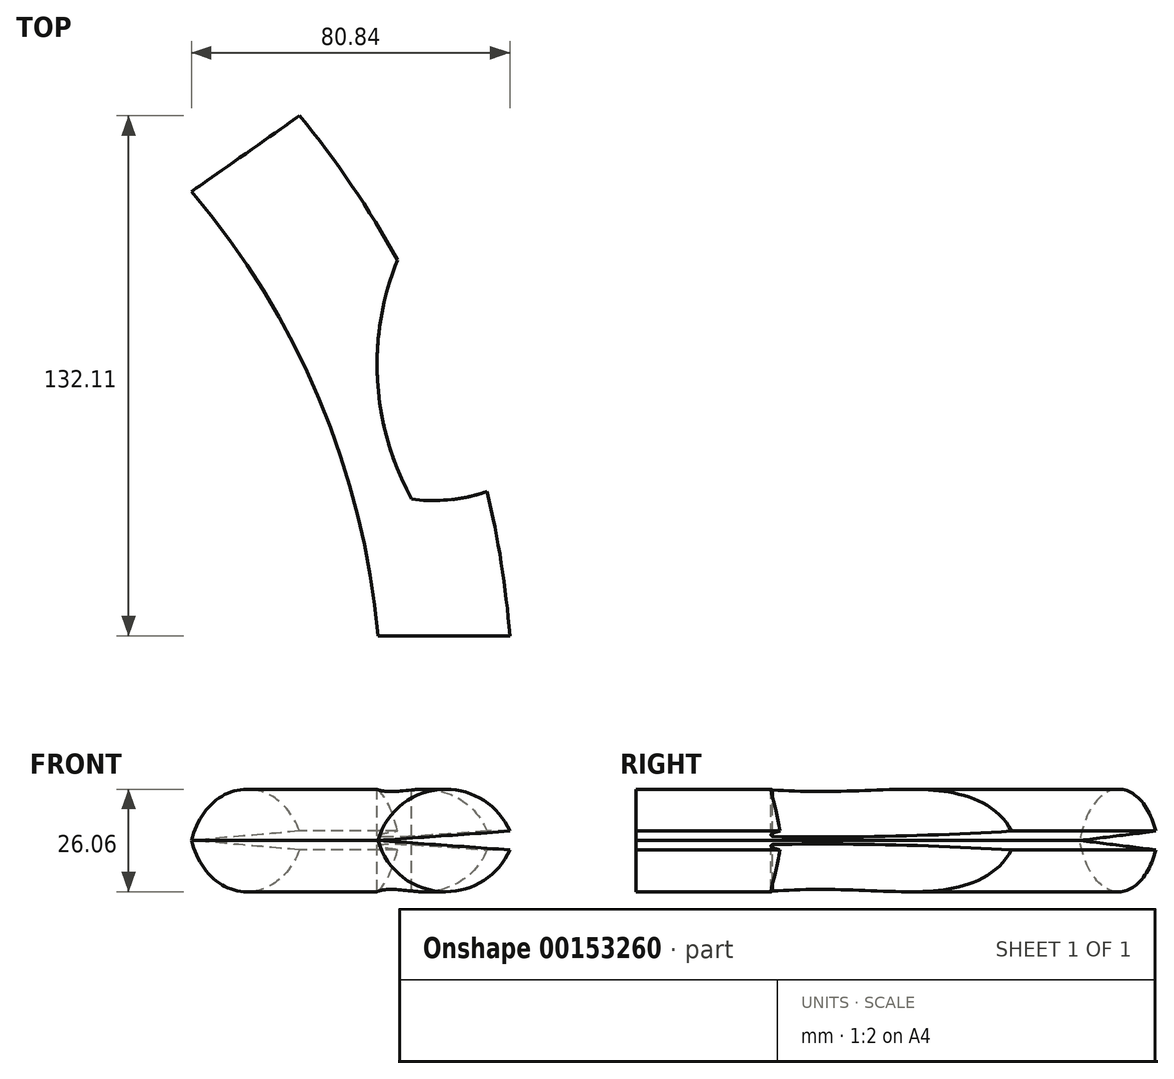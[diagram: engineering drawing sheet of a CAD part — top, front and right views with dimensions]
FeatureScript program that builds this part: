
annotation { "Feature Type Name" : "Feature", "Feature Type Description" : "" }
export const myFeature = defineFeature(function(context is Context, id is Id, definition is map)
    precondition{}
    {
        {
            var Q0;
            Q0=qCreatedBy(makeId("Front.planeOp"),FACE);
            var sketch = newSketch(context, id + "F0", { "sketchPlane" : qUnion([Q0])});
            skArc(sketch, "E0", {"start": v(19.52, 2.39) * mm, "mid": v(1.94, 12.98) * mm, "end": v(-13.96, 0) * mm});
            skLineSegment(sketch, "E1", {"start": v(19.52, 2.39) * mm, "end": v(-13.96, 0) * mm});
            skSolve(sketch);
        }
        {
            var Q0;
            Q0=qCreatedBy(makeId("Top.planeOp"),FACE);
            var sketch = newSketch(context, id + "F1", { "sketchPlane" : qUnion([Q0])});
            skArc(sketch, "E2", {"start": v(55.51, 105.68) * mm, "mid": v(16.55, 59.1) * mm, "end": v(2.58, 0) * mm});
            skArc(sketch, "E3", {"start": v(2.58, 0) * mm, "mid": v(-13.16, 65.07) * mm, "end": v(-47.79, 122.36) * mm});
            skSolve(sketch);
        }
        {
            var Q0;
            Q0=makeQuery(id+"F0.imprint","IMPRINT",FACE,{"disambiguationData":[TD([[makeQuery(id+"F0.imprint","IMPRINT",EDGE,{"derivedFrom":sQuery(id+"F0.wireOp",EDGE,"E0")}),1.0]])]});
            var Q1;
            Q1=sQuery(id+"F1.wireOp",EDGE,"E3");
            sweep(context, id + "F2", {"profiles" : qUnion([Q0]), "path" : qUnion([Q1])});
        }
        {
            var Q0;
            Q0=makeQuery(id+"F2.opSweep","SWEPT_BODY",BODY,{"disambiguationData":[OSD([sQuery(id+"F0.wireOp",EDGE,"E0"),sQuery(id+"F0.wireOp",EDGE,"E1"),sQuery(id+"F1.wireOp",EDGE,"E3")])]});
            var Q1;
            Q1=qCreatedBy(makeId("Top.planeOp"),FACE);
            mirror(context, id + "F3", {"entities" : qUnion([Q0]), "mirrorPlane" : qUnion([Q1])});
        }
        {
            var Q0;
            Q0=qCreatedBy(makeId("Top.planeOp"),FACE);
            var sketch = newSketch(context, id + "F4", { "sketchPlane" : qUnion([Q0])});
            skArc(sketch, "E4", {"start": v(2.34, 114.47) * mm, "mid": v(-13.86, 75.8) * mm, "end": v(-5.43, 34.71) * mm});
            skArc(sketch, "E5", {"start": v(-5.43, 34.71) * mm, "mid": v(26.96, 44.14) * mm, "end": v(41.75, 74.45) * mm});
            skArc(sketch, "E6", {"start": v(41.75, 74.45) * mm, "mid": v(28.68, 101) * mm, "end": v(2.34, 114.47) * mm});
            skSolve(sketch);
        }
        {
            var Q0;
            Q0=makeQuery(id+"F4.imprint","IMPRINT",FACE,{"disambiguationData":[TD([[makeQuery(id+"F4.imprint","IMPRINT",EDGE,{"derivedFrom":sQuery(id+"F4.wireOp",EDGE,"E4")}),1.0]])]});
            extrude(context, id + "F5", {"entities" : qUnion([Q0]), "operationType" : NewBodyOperationType.REMOVE, "endBound" : BoundingType.SYMMETRIC, "oppositeDirection" : true, "depth" : 39.37 * mm});
        }
    });
